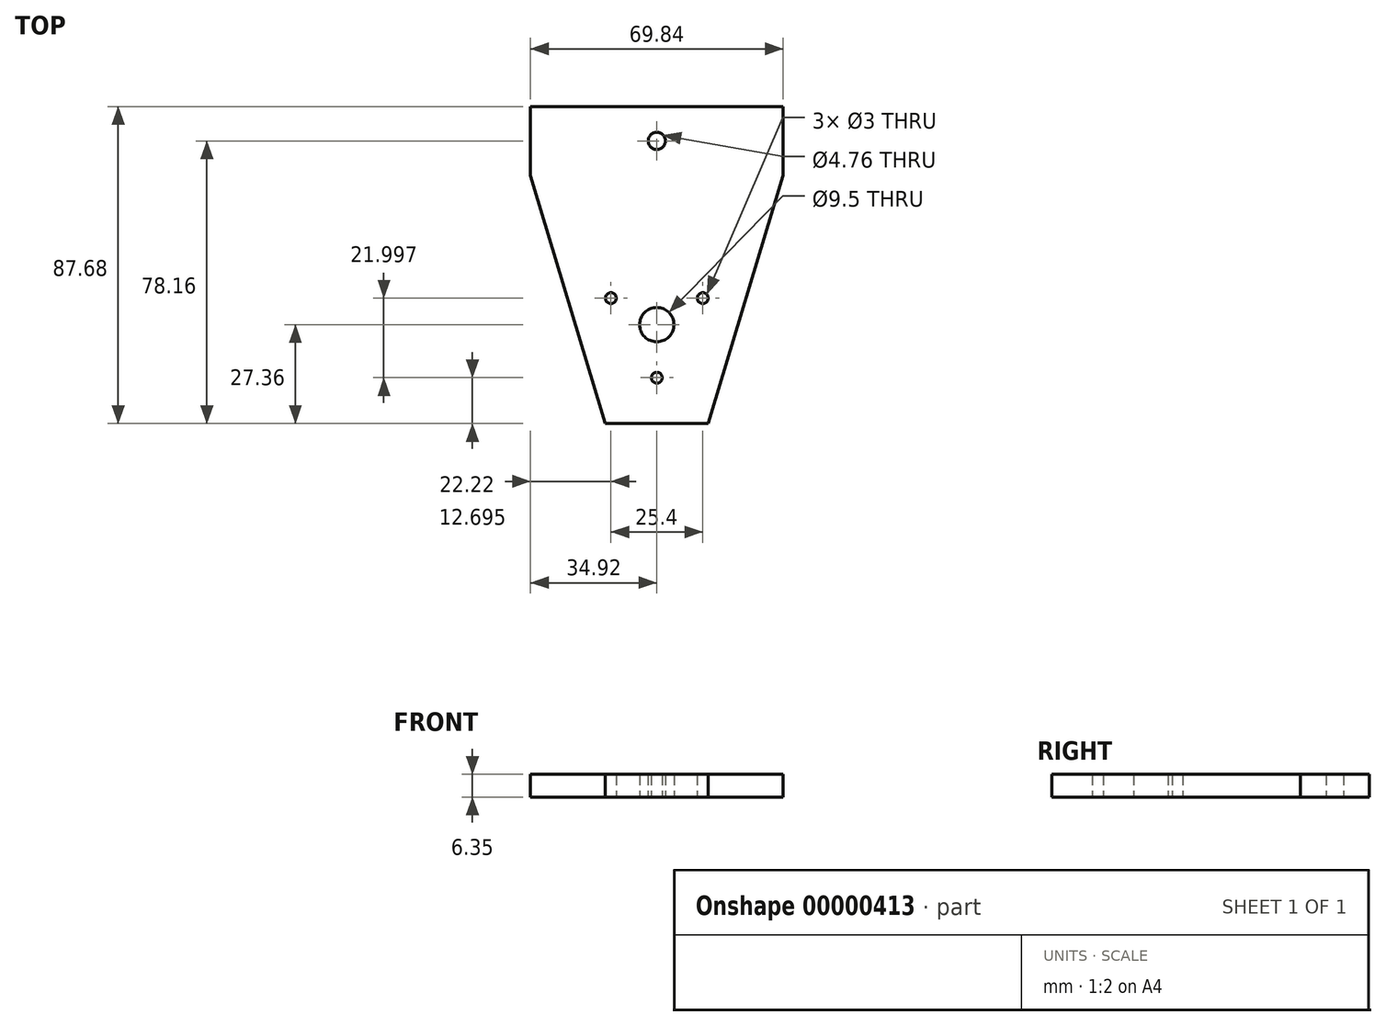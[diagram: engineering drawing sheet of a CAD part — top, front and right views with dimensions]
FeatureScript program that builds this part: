
annotation { "Feature Type Name" : "Feature", "Feature Type Description" : "" }
export const myFeature = defineFeature(function(context is Context, id is Id, definition is map)
    precondition{}
    {
        {
            var Q0;
            Q0=qCreatedBy(makeId("Top.planeOp"),FACE);
            var sketch = newSketch(context, id + "F0", { "sketchPlane" : qUnion([Q0])});
            skCircle(sketch, "E0", {"center": v(0, 0) * mm, "radius": 4.75 * mm});
            skLineSegment(sketch, "E1", {"start": v(-34.92, 60.33) * mm, "end": v(34.93, 60.33) * mm});
            skLineSegment(sketch, "E2", {"start": v(34.93, 60.33) * mm, "end": v(34.93, 41.28) * mm});
            skLineSegment(sketch, "E3", {"start": v(34.93, 41.28) * mm, "end": v(14.2, -27.36) * mm});
            skLineSegment(sketch, "E4", {"start": v(14.2, -27.36) * mm, "end": v(-14.2, -27.36) * mm});
            skLineSegment(sketch, "E5", {"start": v(-14.2, -27.36) * mm, "end": v(-34.92, 41.28) * mm});
            skLineSegment(sketch, "E6", {"start": v(-34.92, 41.28) * mm, "end": v(-34.92, 60.33) * mm});
            skCircle(sketch, "E7", {"center": v(0, 50.8) * mm, "radius": 2.38 * mm});
            skCircle(sketch, "E8", {"center": v(-12.7, 7.33) * mm, "radius": 1.5 * mm});
            skCircle(sketch, "E9", {"center": v(0, -14.66) * mm, "radius": 1.5 * mm});
            skCircle(sketch, "E10", {"center": v(12.7, 7.33) * mm, "radius": 1.5 * mm});
            skLineSegment(sketch, "E11", {"start": v(-12.7, 7.33) * mm, "end": v(12.7, 7.33) * mm, "construction": true});
            skLineSegment(sketch, "E12", {"start": v(0, -14.66) * mm, "end": v(-12.7, 7.33) * mm, "construction": true});
            skLineSegment(sketch, "E13", {"start": v(12.7, 7.33) * mm, "end": v(0, -14.66) * mm, "construction": true});
            skLineSegment(sketch, "E14", {"start": v(-6.35, -3.67) * mm, "end": v(0, 0) * mm, "construction": true});
            skSolve(sketch);
        }
        {
            var Q0;
            Q0=makeQuery(id+"F0.imprint","IMPRINT",FACE,{"disambiguationData":[TD([[makeQuery(id+"F0.imprint","IMPRINT",EDGE,{"derivedFrom":sQuery(id+"F0.wireOp",EDGE,"E0")}),-1.0]])]});
            extrude(context, id + "F1", {"entities" : qUnion([Q0]), "depth" : 6.35 * mm});
        }
    });
